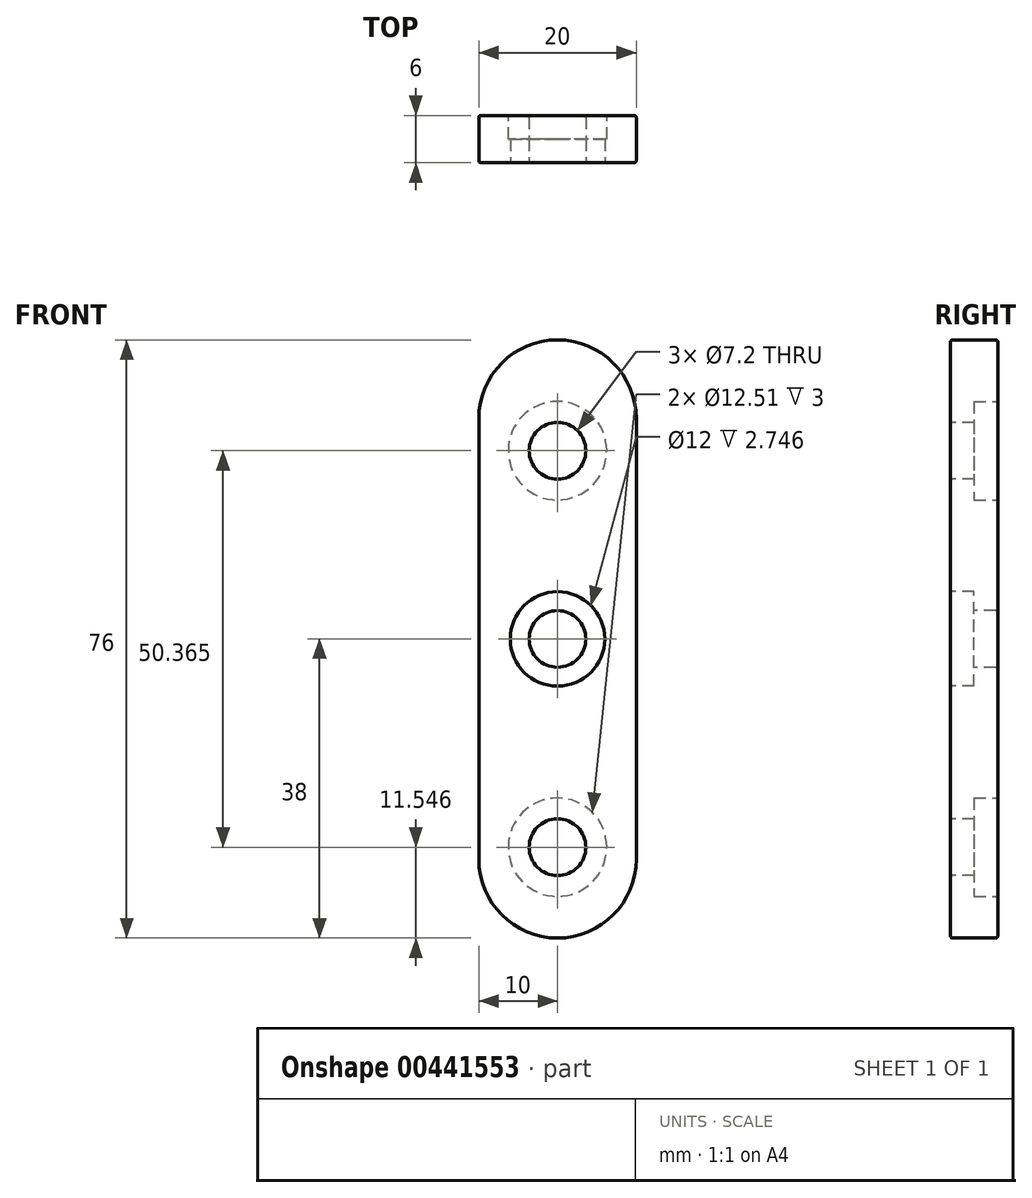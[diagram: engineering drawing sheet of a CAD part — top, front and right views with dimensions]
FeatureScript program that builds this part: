
annotation { "Feature Type Name" : "Feature", "Feature Type Description" : "" }
export const myFeature = defineFeature(function(context is Context, id is Id, definition is map)
    precondition{}
    {
        {
            var Q0;
            Q0=qCreatedBy(makeId("Front.planeOp"),FACE);
            var sketch = newSketch(context, id + "F0", { "sketchPlane" : qUnion([Q0])});
            skLineSegment(sketch, "E0.left", {"start": v(10, -28) * mm, "end": v(10, 28) * mm});
            skLineSegment(sketch, "E0.right", {"start": v(-10, -28) * mm, "end": v(-10, 28) * mm});
            skPoint(sketch, "E0.middle", {"position": v(0, 0) * mm});
            skArc(sketch, "E1", {"start": v(10, 28) * mm, "mid": v(0, 38) * mm, "end": v(-10, 28) * mm});
            skArc(sketch, "E2", {"start": v(-10, -28) * mm, "mid": v(0, -38) * mm, "end": v(10, -28) * mm});
            skCircle(sketch, "E3", {"center": v(0, 23.91) * mm, "radius": 3.6 * mm});
            skCircle(sketch, "E4", {"center": v(0, -26.45) * mm, "radius": 3.6 * mm});
            skCircle(sketch, "E5", {"center": v(0, 0) * mm, "radius": 3.6 * mm});
            skSolve(sketch);
        }
        {
            var Q0;
            Q0=makeQuery(id+"F0.imprint","IMPRINT",FACE,{"disambiguationData":[TD([[makeQuery(id+"F0.imprint","IMPRINT",EDGE,{"derivedFrom":sQuery(id+"F0.wireOp",EDGE,"E0.left")}),1.0]])]});
            extrude(context, id + "F1", {"entities" : qUnion([Q0]), "oppositeDirection" : true, "depth" : 6 * mm});
        }
        {
            var Q0;
            Q0=qCreatedBy(makeId("Front.planeOp"),FACE);
            var sketch = newSketch(context, id + "F2", { "sketchPlane" : qUnion([Q0])});
            skCircle(sketch, "E6", {"center": v(0, 0) * mm, "radius": 6 * mm});
            skSolve(sketch);
        }
        {
            var Q0;
            Q0 = qSketchRegion(id + "F2", true);
            extrude(context, id + "F3", {"entities" : qUnion([Q0]), "operationType" : NewBodyOperationType.REMOVE, "oppositeDirection" : true, "depth" : 3 * mm});
        }
        {
            var Q0;
            Q0=makeQuery(id+"F1.opExtrude","CAP_FACE",FACE,{"disambiguationData":[OSD([sQuery(id+"F0.wireOp",EDGE,"E0.left"),sQuery(id+"F0.wireOp",EDGE,"E0.right"),sQuery(id+"F0.wireOp",EDGE,"E1"),sQuery(id+"F0.wireOp",EDGE,"E2"),sQuery(id+"F0.wireOp",EDGE,"E3"),sQuery(id+"F0.wireOp",EDGE,"E4"),sQuery(id+"F0.wireOp",EDGE,"E5")])],"isStart":true});
            var Q1;
            Q1=makeQuery(id+"F1.opExtrude","CAP_FACE",FACE,{"disambiguationData":[OSD([sQuery(id+"F0.wireOp",EDGE,"E0.left"),sQuery(id+"F0.wireOp",EDGE,"E0.right"),sQuery(id+"F0.wireOp",EDGE,"E1"),sQuery(id+"F0.wireOp",EDGE,"E2"),sQuery(id+"F0.wireOp",EDGE,"E3"),sQuery(id+"F0.wireOp",EDGE,"E4"),sQuery(id+"F0.wireOp",EDGE,"E5")])],"isStart":false});
            fillet(context, id + "F4", {"entities" : qUnion([Q0, Q1]), "radius" : 0.25 * mm, "tangentPropagation" : true, "allowEdgeOverflow" : false});
        }
        {
            var Q0;
            Q0=makeQuery(id+"F1.opExtrude","CAP_FACE",FACE,{"disambiguationData":[OSD([sQuery(id+"F0.wireOp",EDGE,"E0.left"),sQuery(id+"F0.wireOp",EDGE,"E0.right"),sQuery(id+"F0.wireOp",EDGE,"E1"),sQuery(id+"F0.wireOp",EDGE,"E2"),sQuery(id+"F0.wireOp",EDGE,"E3"),sQuery(id+"F0.wireOp",EDGE,"E4"),sQuery(id+"F0.wireOp",EDGE,"E5")])],"isStart":false});
            var sketch = newSketch(context, id + "F5", { "sketchPlane" : qUnion([Q0])});
            skCircle(sketch, "E7", {"center": v(0, 23.91) * mm, "radius": 6.25 * mm});
            skCircle(sketch, "E8", {"center": v(0, -26.45) * mm, "radius": 6.25 * mm});
            skSolve(sketch);
        }
        {
            var Q0;
            Q0 = qSketchRegion(id + "F5", true);
            extrude(context, id + "F6", {"entities" : qUnion([Q0]), "operationType" : NewBodyOperationType.REMOVE, "oppositeDirection" : true, "depth" : 3 * mm});
        }
    });
